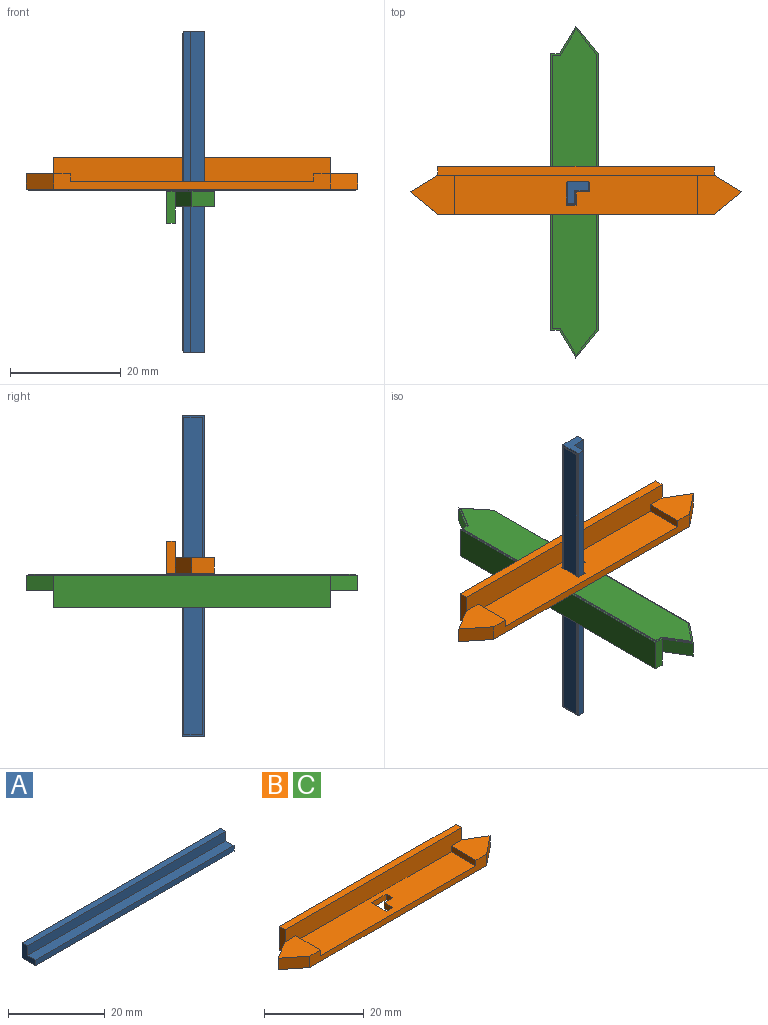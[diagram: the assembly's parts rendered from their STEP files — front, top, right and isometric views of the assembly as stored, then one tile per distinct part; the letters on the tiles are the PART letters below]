
ASSEMBLY  parts=3 mates=4
PART A: 13 faces, bbox 58x4x4 mm
  f0: plane 58x3.8mm, normal (0,1,0), area 220.4mm2, adj f1,f5,f6,f11
  f1: plane 58x1.6mm, normal (0,0,1), area 92.8mm2, adj f0,f2,f5,f6
  f2: plane 58x2.4mm, normal (0,-1,0), area 139.2mm2, adj f1,f3,f5,f6
  f3: plane 58x2.4mm, normal (0,0,1), area 139.2mm2, adj f2,f4,f5,f6
  f4: plane 58x1.4mm, normal (0,-1,0), area 81.2mm2, adj f3,f5,f6,f11
  f5: plane 4x3.8mm, normal (1,0,0), area 9.4mm2, adj f0,f1,f2,f3,f4,f11
  f6: plane 4x3.8mm, normal (-1,0,0), area 9.4mm2, adj f0,f1,f2,f3,f4,f11
  f7: plane 57.4x0.2mm, normal (0,-1,0), area 11.5mm2, adj f8,f10,f11,f12
  f8: plane 3.4x0.2mm, normal (1,0,0), area 0.7mm2, adj f7,f9,f11,f12
  f9: plane 57.4x0.2mm, normal (0,1,0), area 11.5mm2, adj f8,f10,f11,f12
  f10: plane 3.4x0.2mm, normal (-1,0,0), area 0.7mm2, adj f7,f9,f11,f12
  f11: plane 58x4mm, normal (0,0,-1), area 36.8mm2, adj f0,f4,f5,f6,f7,f8,f9,f10
  f12: plane 57.4x3.4mm, normal (0,0,-1), area 195.2mm2, adj f7,f8,f9,f10
PART B: 38 faces, bbox 60x8.6x6 mm
  f0: plane 5.8x1.6mm, normal (1,0,0), area 9.3mm2, adj f9,f10,f13,f14,f29
  f1: plane 5.8x1.6mm, normal (-1,0,0), area 9.3mm2, adj f8,f10,f13,f14,f29
  f2: plane 2.4x1.4mm, normal (0,1,0), area 3.4mm2, adj f3,f7,f12,f37
  f3: plane 2.4x1.4mm, normal (-1,0,0), area 3.4mm2, adj f2,f4,f12,f37
  f4: plane 1.8x1.4mm, normal (0,1,0), area 2.5mm2, adj f3,f5,f12,f37
  f5: plane 4.2x1.4mm, normal (1,0,0), area 5.9mm2, adj f4,f6,f12,f37
  f6: plane 4.2x1.4mm, normal (0,-1,0), area 5.9mm2, adj f5,f7,f12,f37
  f7: plane 1.8x1.4mm, normal (-1,0,0), area 2.5mm2, adj f2,f6,f12,f37
  f8: plane 5x3mm, normal (-0.51,0.86,0), area 16.3mm2, adj f1,f15,f17,f29
  f9: plane 5x3mm, normal (0.51,0.86,0), area 16.3mm2, adj f0,f19,f20,f29
  f10: plane 50x4.4mm, normal (0,-1,0), area 211.6mm2, adj f0,f1,f12,f14,f16,f17,f18,f20
  f11: plane 50x2.8mm, normal (0,-1,0), area 78.4mm2, adj f12,f15,f16,f17,f18,f19,f20,f29
  f12: plane 44x7mm, normal (0,0,1), area 296.1mm2, adj f2,f3,f4,f5,f6,f7,f10,f11
  f13: plane 50x5.8mm, normal (0,1,0), area 290mm2, adj f0,f1,f14,f29
  f14: plane 50x1.6mm, normal (0,0,1), area 80mm2, adj f0,f1,f10,f13
  f15: plane 5x4mm, normal (-0.62,-0.78,0), area 17.9mm2, adj f8,f11,f17,f29
  f16: plane 7x1.4mm, normal (1,0,0), area 9.8mm2, adj f10,f11,f12,f17
  f17: plane 8x7mm, normal (0,0,1), area 38.5mm2, adj f8,f10,f11,f15,f16
  f18: plane 7x1.4mm, normal (-1,0,0), area 9.8mm2, adj f10,f11,f12,f20
  f19: plane 5x4mm, normal (0.62,-0.78,0), area 17.9mm2, adj f9,f11,f20,f29
  f20: plane 8x7mm, normal (0,0,1), area 38.5mm2, adj f9,f10,f11,f18,f19
  f21: plane 4.58x3.66mm, normal (0.62,-0.78,0), area 1.2mm2, adj f22,f28,f29,f30
  f22: plane 4.78x2.87mm, normal (0.51,0.86,0), area 1.1mm2, adj f21,f23,f29,f30
  f23: plane 1.47x0.2mm, normal (1,0,0), area 0.3mm2, adj f22,f24,f29,f30
  f24: plane 49.4x0.2mm, normal (0,1,0), area 9.9mm2, adj f23,f25,f29,f30
  f25: plane 1.47x0.2mm, normal (-1,0,0), area 0.3mm2, adj f24,f26,f29,f30
  f26: plane 4.78x2.87mm, normal (-0.51,0.86,0), area 1.1mm2, adj f25,f27,f29,f30
  f27: plane 4.58x3.66mm, normal (-0.62,-0.78,0), area 1.2mm2, adj f26,f28,f29,f30
  f28: plane 49.79x0.2mm, normal (0,-1,0), area 10mm2, adj f21,f27,f29,f30
  f29: plane 60x8.6mm, normal (0,0,-1), area 37.9mm2, adj f0,f1,f8,f9,f11,f13,f15,f19
  f30: plane 58.95x8mm, normal (0,0,-1), area 409.8mm2, adj f21,f22,f23,f24,f25,f26,f27,f28
  f31: plane 2.4x0.2mm, normal (-1,0,0), area 0.5mm2, adj f30,f32,f36,f37
  f32: plane 2.4x0.2mm, normal (0,1,0), area 0.5mm2, adj f30,f31,f33,f37
  f33: plane 4.8x0.2mm, normal (1,0,0), area 1mm2, adj f30,f32,f34,f37
  f34: plane 4.8x0.2mm, normal (0,-1,0), area 1mm2, adj f30,f33,f35,f37
  f35: plane 2.4x0.2mm, normal (-1,0,0), area 0.5mm2, adj f30,f34,f36,f37
  f36: plane 2.4x0.2mm, normal (0,1,0), area 0.5mm2, adj f30,f31,f35,f37
  f37: plane 4.8x4.8mm, normal (0,0,-1), area 5.4mm2, adj f2,f3,f4,f5,f6,f7,f31,f32
PART C: same geometry as B
PLACE A rot(axis=(0,1,0),90deg) t=(-1.8,1.8,-0.31)mm
PLACE B at identity fixed
PLACE C rot(axis=(0.71,-0.71,0),180deg) t=(0,0,0)mm
MATE planar B.f6 <-> A.f0  axis (0,-1,0) through (0.3,1.8,0.9)mm
MATE planar B.f5 <-> A.f12  axis (1,0,0) through (-1.8,-0.3,0.9)mm
MATE planar A.f0 <-> C.f5  axis (0,1,0) through (0.3,1.8,-0.31)mm
MATE planar A.f12 <-> C.f6  axis (-1,0,0) through (-1.8,-0.2,-0.31)mm
